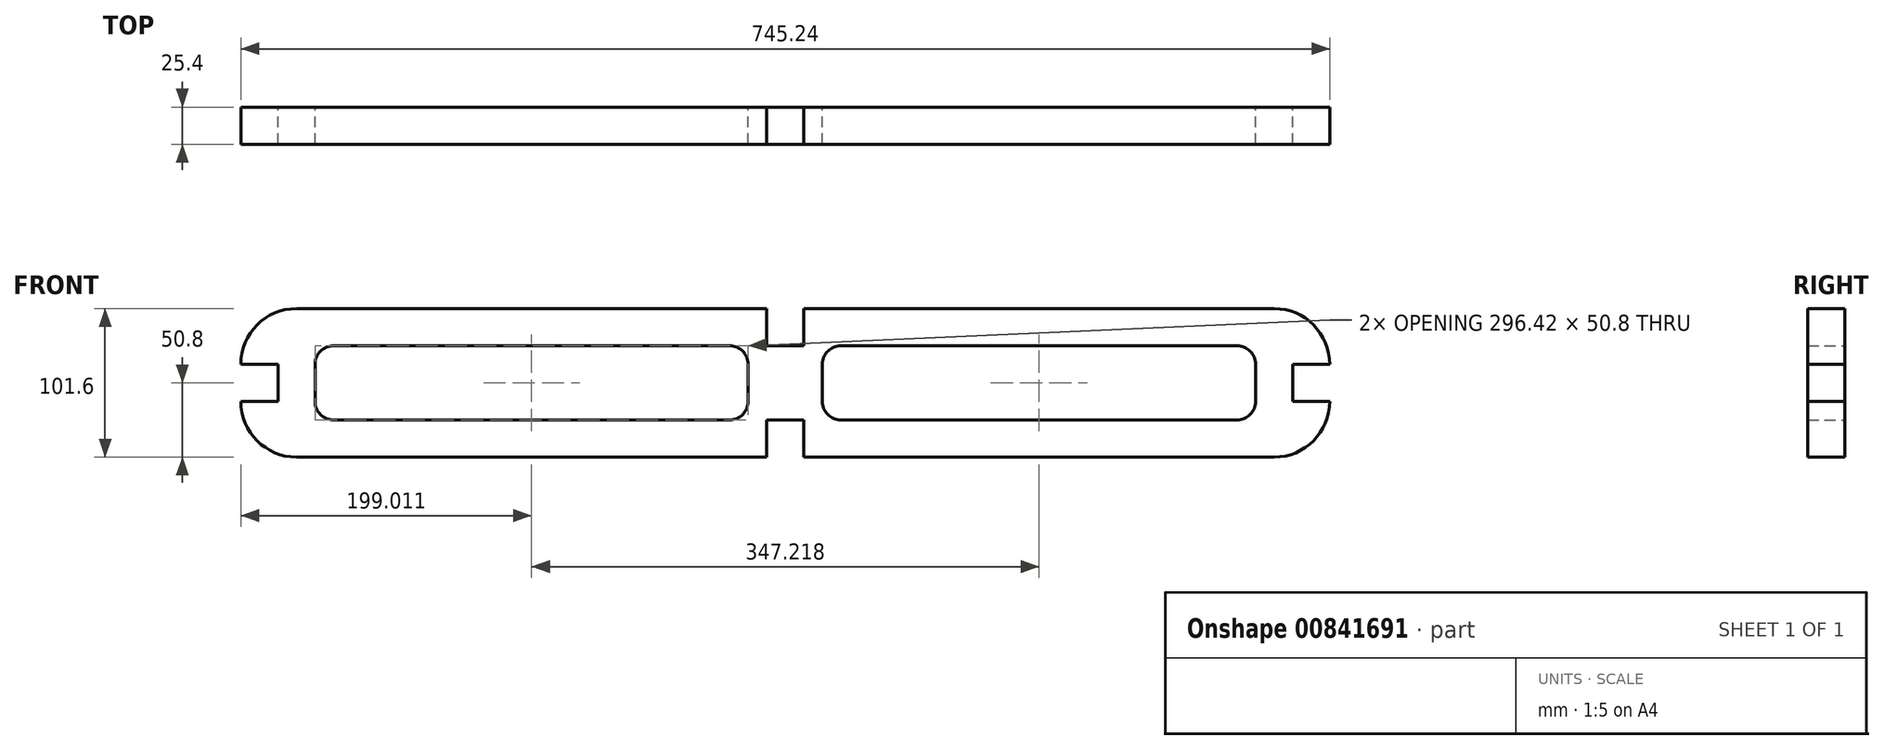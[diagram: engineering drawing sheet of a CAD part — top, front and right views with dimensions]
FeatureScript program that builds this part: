
annotation { "Feature Type Name" : "Feature", "Feature Type Description" : "" }
export const myFeature = defineFeature(function(context is Context, id is Id, definition is map)
    precondition{}
    {
        {
            var Q0;
            Q0=qCreatedBy(makeId("Front.planeOp"),FACE);
            var sketch = newSketch(context, id + "F0", { "sketchPlane" : qUnion([Q0])});
            skLineSegment(sketch, "E0", {"start": v(0, 0) * mm, "end": v(-347.22, 0) * mm, "construction": true});
            skLineSegment(sketch, "E1", {"start": v(0, 0) * mm, "end": v(0, 50.8) * mm, "construction": true});
            skLineSegment(sketch, "E2", {"start": v(0, 0) * mm, "end": v(0, -50.8) * mm, "construction": true});
            skLineSegment(sketch, "E3", {"start": v(-347.22, 12.7) * mm, "end": v(-347.22, -12.7) * mm});
            skLineSegment(sketch, "E4", {"start": v(-347.22, 12.7) * mm, "end": v(-372.62, 12.7) * mm});
            skLineSegment(sketch, "E5", {"start": v(-347.22, -12.7) * mm, "end": v(-372.62, -12.7) * mm});
            skLineSegment(sketch, "E6", {"start": v(-372.62, 12.7) * mm, "end": v(-372.62, -12.7) * mm, "construction": true});
            skLineSegment(sketch, "E7", {"start": v(0, 50.8) * mm, "end": v(-334.52, 50.8) * mm});
            skLineSegment(sketch, "E8", {"start": v(-334.52, 50.8) * mm, "end": v(-334.52, -50.8) * mm, "construction": true});
            skLineSegment(sketch, "E9", {"start": v(-334.52, -50.8) * mm, "end": v(0, -50.8) * mm});
            skArc(sketch, "E10", {"start": v(-334.52, 50.8) * mm, "mid": v(-361.46, 39.64) * mm, "end": v(-372.62, 12.7) * mm});
            skArc(sketch, "E11", {"start": v(-372.62, -12.7) * mm, "mid": v(-361.46, -39.64) * mm, "end": v(-334.52, -50.8) * mm});
            skLineSegment(sketch, "E12.bottom", {"start": v(-309.12, -25.4) * mm, "end": v(-38.1, -25.4) * mm});
            skLineSegment(sketch, "E12.top", {"start": v(-309.12, 25.4) * mm, "end": v(-38.1, 25.4) * mm});
            skLineSegment(sketch, "E12.left", {"start": v(-321.82, -12.7) * mm, "end": v(-321.82, 12.7) * mm});
            skLineSegment(sketch, "E12.right", {"start": v(-25.4, -12.7) * mm, "end": v(-25.4, 12.7) * mm});
            skPoint(sketch, "E13.visualSharp", {"position": v(-321.82, 25.4) * mm});
            skArc(sketch, "E13.filletArc", {"start": v(-309.12, 25.4) * mm, "mid": v(-318.1, 21.68) * mm, "end": v(-321.82, 12.7) * mm});
            skPoint(sketch, "E14.visualSharp", {"position": v(-321.82, -25.4) * mm});
            skArc(sketch, "E14.filletArc", {"start": v(-321.82, -12.7) * mm, "mid": v(-318.1, -21.68) * mm, "end": v(-309.12, -25.4) * mm});
            skPoint(sketch, "E15.visualSharp", {"position": v(-25.4, 25.4) * mm});
            skArc(sketch, "E15.filletArc", {"start": v(-25.4, 12.7) * mm, "mid": v(-29.12, 21.68) * mm, "end": v(-38.1, 25.4) * mm});
            skPoint(sketch, "E16.visualSharp", {"position": v(-25.4, -25.4) * mm});
            skArc(sketch, "E16.filletArc", {"start": v(-38.1, -25.4) * mm, "mid": v(-29.12, -21.68) * mm, "end": v(-25.4, -12.7) * mm});
            skLineSegment(sketch, "E17.MirrorCS", {"start": v(0, 50.8) * mm, "end": v(334.52, 50.8) * mm});
            skLineSegment(sketch, "E18.MirrorCS", {"start": v(334.52, -50.8) * mm, "end": v(0, -50.8) * mm});
            skArc(sketch, "E19.MirrorCS", {"start": v(372.62, -12.7) * mm, "mid": v(361.46, -39.64) * mm, "end": v(334.52, -50.8) * mm});
            skLineSegment(sketch, "E20.MirrorCS", {"start": v(347.22, -12.7) * mm, "end": v(372.62, -12.7) * mm});
            skLineSegment(sketch, "E21.MirrorCS", {"start": v(347.22, 12.7) * mm, "end": v(347.22, -12.7) * mm});
            skLineSegment(sketch, "E22.MirrorCS", {"start": v(347.22, 12.7) * mm, "end": v(372.62, 12.7) * mm});
            skArc(sketch, "E23.MirrorCS", {"start": v(334.52, 50.8) * mm, "mid": v(361.46, 39.64) * mm, "end": v(372.62, 12.7) * mm});
            skLineSegment(sketch, "E24.MirrorCS", {"start": v(321.82, -12.7) * mm, "end": v(321.82, 12.7) * mm});
            skArc(sketch, "E25.MirrorCS", {"start": v(309.12, 25.4) * mm, "mid": v(318.1, 21.68) * mm, "end": v(321.82, 12.7) * mm});
            skArc(sketch, "E26.MirrorCS", {"start": v(321.82, -12.7) * mm, "mid": v(318.1, -21.68) * mm, "end": v(309.12, -25.4) * mm});
            skLineSegment(sketch, "E27.MirrorCS", {"start": v(309.12, -25.4) * mm, "end": v(38.1, -25.4) * mm});
            skLineSegment(sketch, "E28.MirrorCS", {"start": v(309.12, 25.4) * mm, "end": v(38.1, 25.4) * mm});
            skArc(sketch, "E29.MirrorCS", {"start": v(25.4, 12.7) * mm, "mid": v(29.12, 21.68) * mm, "end": v(38.1, 25.4) * mm});
            skLineSegment(sketch, "E30.MirrorCS", {"start": v(25.4, -12.7) * mm, "end": v(25.4, 12.7) * mm});
            skArc(sketch, "E31.MirrorCS", {"start": v(38.1, -25.4) * mm, "mid": v(29.12, -21.68) * mm, "end": v(25.4, -12.7) * mm});
            skSolve(sketch);
        }
        {
            var Q0;
            Q0 = qSketchRegion(id + "F0", true);
            extrude(context, id + "F1", {"entities" : qUnion([Q0]), "depth" : 25.4 * mm, "offsetDistance" : 25.4 * mm});
        }
        {
            var Q0;
            Q0=makeQuery(id+"F1.opExtrude","CAP_FACE",FACE,{"disambiguationData":[OSD([sQuery(id+"F0.wireOp",EDGE,"E3"),sQuery(id+"F0.wireOp",EDGE,"E4"),sQuery(id+"F0.wireOp",EDGE,"E5"),sQuery(id+"F0.wireOp",EDGE,"E7"),sQuery(id+"F0.wireOp",EDGE,"E9"),sQuery(id+"F0.wireOp",EDGE,"E10"),sQuery(id+"F0.wireOp",EDGE,"E11"),sQuery(id+"F0.wireOp",EDGE,"E12.bottom"),sQuery(id+"F0.wireOp",EDGE,"E12.top"),sQuery(id+"F0.wireOp",EDGE,"E12.left"),sQuery(id+"F0.wireOp",EDGE,"E12.right"),sQuery(id+"F0.wireOp",EDGE,"E13.filletArc"),sQuery(id+"F0.wireOp",EDGE,"E14.filletArc"),sQuery(id+"F0.wireOp",EDGE,"E15.filletArc"),sQuery(id+"F0.wireOp",EDGE,"E16.filletArc"),sQuery(id+"F0.wireOp",EDGE,"E17.MirrorCS"),sQuery(id+"F0.wireOp",EDGE,"E18.MirrorCS"),sQuery(id+"F0.wireOp",EDGE,"E19.MirrorCS"),sQuery(id+"F0.wireOp",EDGE,"E20.MirrorCS"),sQuery(id+"F0.wireOp",EDGE,"E21.MirrorCS"),sQuery(id+"F0.wireOp",EDGE,"E22.MirrorCS"),sQuery(id+"F0.wireOp",EDGE,"E23.MirrorCS"),sQuery(id+"F0.wireOp",EDGE,"E24.MirrorCS"),sQuery(id+"F0.wireOp",EDGE,"E25.MirrorCS"),sQuery(id+"F0.wireOp",EDGE,"E26.MirrorCS"),sQuery(id+"F0.wireOp",EDGE,"E27.MirrorCS"),sQuery(id+"F0.wireOp",EDGE,"E28.MirrorCS"),sQuery(id+"F0.wireOp",EDGE,"E29.MirrorCS"),sQuery(id+"F0.wireOp",EDGE,"E30.MirrorCS"),sQuery(id+"F0.wireOp",EDGE,"E31.MirrorCS")])],"isStart":false});
            var sketch = newSketch(context, id + "F2", { "sketchPlane" : qUnion([Q0])});
            skLineSegment(sketch, "E32.bottom", {"start": v(-12.7, 50.8) * mm, "end": v(12.7, 50.8) * mm});
            skLineSegment(sketch, "E32.top", {"start": v(-12.7, 25.4) * mm, "end": v(12.7, 25.4) * mm});
            skLineSegment(sketch, "E32.left", {"start": v(-12.7, 50.8) * mm, "end": v(-12.7, 25.4) * mm});
            skLineSegment(sketch, "E32.right", {"start": v(12.7, 50.8) * mm, "end": v(12.7, 25.4) * mm});
            skLineSegment(sketch, "E33.bottom", {"start": v(-12.7, -50.8) * mm, "end": v(12.7, -50.8) * mm});
            skLineSegment(sketch, "E33.top", {"start": v(-12.7, -25.4) * mm, "end": v(12.7, -25.4) * mm});
            skLineSegment(sketch, "E33.left", {"start": v(-12.7, -50.8) * mm, "end": v(-12.7, -25.4) * mm});
            skLineSegment(sketch, "E33.right", {"start": v(12.7, -50.8) * mm, "end": v(12.7, -25.4) * mm});
            skLineSegment(sketch, "E34", {"start": v(0, 25.4) * mm, "end": v(0, 0) * mm, "construction": true});
            skLineSegment(sketch, "E35", {"start": v(0, 0) * mm, "end": v(0, -25.4) * mm, "construction": true});
            skSolve(sketch);
        }
        {
            var Q0;
            Q0 = qSketchRegion(id + "F2", true);
            extrude(context, id + "F3", {"entities" : qUnion([Q0]), "operationType" : NewBodyOperationType.REMOVE, "oppositeDirection" : true, "depth" : 25.4 * mm, "offsetDistance" : 25.4 * mm});
        }
    });
